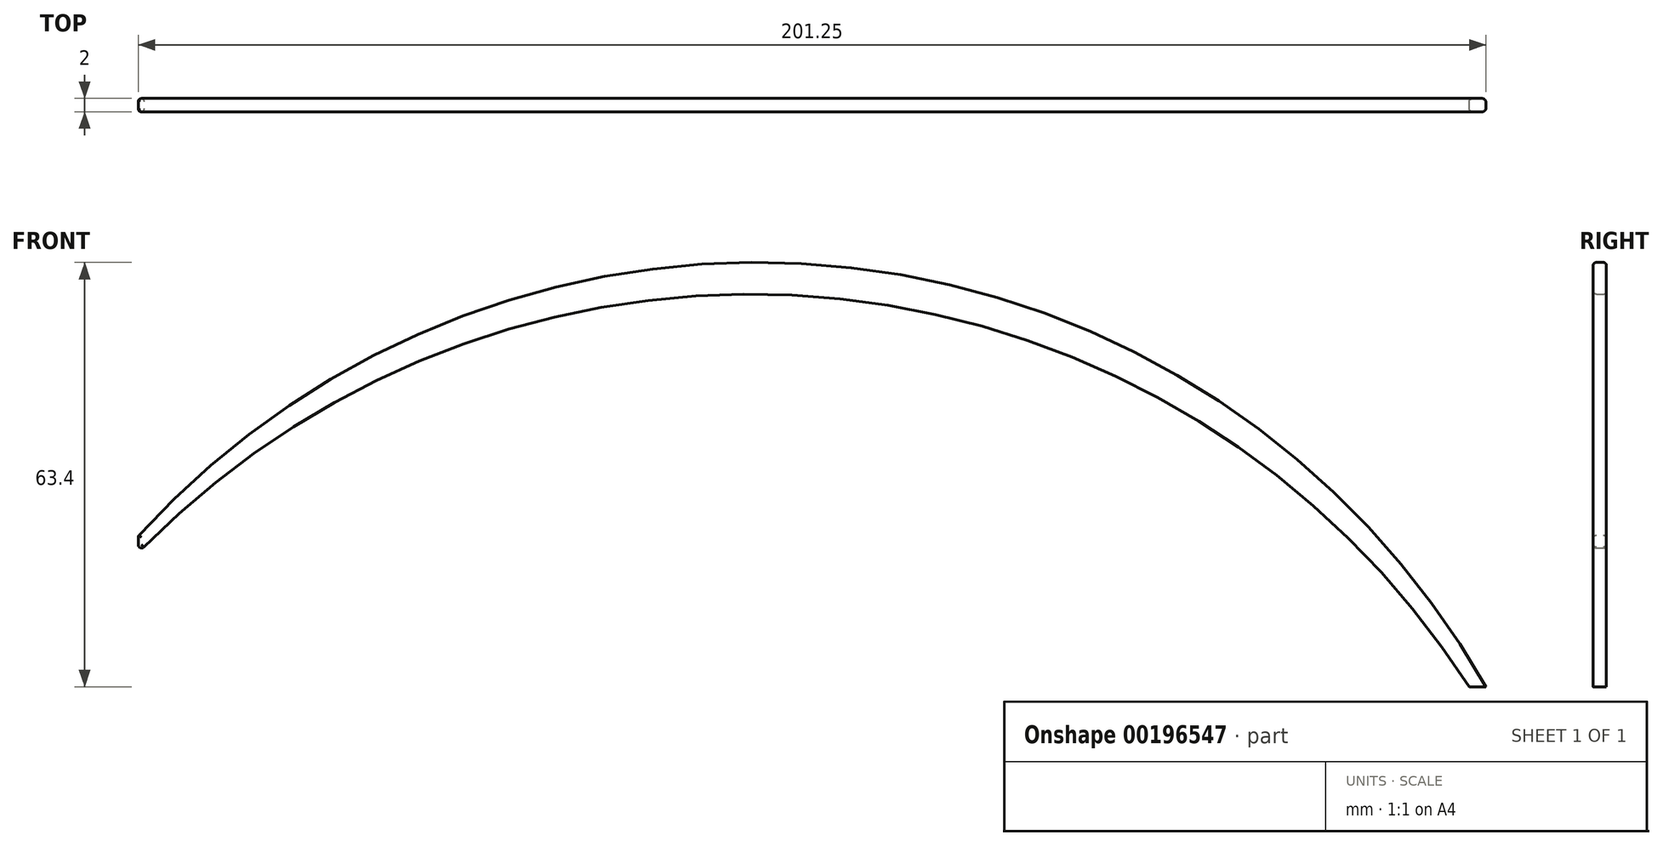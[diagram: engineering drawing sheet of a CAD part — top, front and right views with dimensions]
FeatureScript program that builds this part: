
annotation { "Feature Type Name" : "Feature", "Feature Type Description" : "" }
export const myFeature = defineFeature(function(context is Context, id is Id, definition is map)
    precondition{}
    {
        {
            var Q0;
            Q0=qCreatedBy(makeId("Front.planeOp"),FACE);
            var sketch = newSketch(context, id + "F0", { "sketchPlane" : qUnion([Q0])});
            skLineSegment(sketch, "E0", {"start": v(-1.25, 0) * mm, "end": v(1.25, 0) * mm});
            skLineSegment(sketch, "E1", {"start": v(-200, 22.5) * mm, "end": v(-200, 20) * mm});
            skArc(sketch, "E2", {"start": v(1.25, 0) * mm, "mid": v(-93.63, 62.63) * mm, "end": v(-200, 22.5) * mm});
            skArc(sketch, "E3", {"start": v(-1.25, 0) * mm, "mid": v(-95.8, 58) * mm, "end": v(-200, 20) * mm});
            skSolve(sketch);
        }
        {
            var Q0;
            Q0 = qSketchRegion(id + "F0", true);
            extrude(context, id + "F1", {"entities" : qUnion([Q0]), "depth" : 2 * mm});
        }
        {
            var Q0;
            Q0=makeQuery(id+"F1.opExtrude","CAP_EDGE",EDGE,{"disambiguationData":[OSD([sQuery(id+"F0.wireOp",EDGE,"E2")])],"isStart":false});
            var Q1;
            Q1=makeQuery(id+"F1.opExtrude","CAP_EDGE",EDGE,{"disambiguationData":[OSD([sQuery(id+"F0.wireOp",EDGE,"E3")])],"isStart":false});
            var Q2;
            Q2=makeQuery(id+"F1.opExtrude","CAP_EDGE",EDGE,{"disambiguationData":[OSD([sQuery(id+"F0.wireOp",EDGE,"E2")])],"isStart":true});
            var Q3;
            Q3=makeQuery(id+"F1.opExtrude","CAP_EDGE",EDGE,{"disambiguationData":[OSD([sQuery(id+"F0.wireOp",EDGE,"E3")])],"isStart":true});
            fillet(context, id + "F2", {"entities" : qUnion([Q0, Q1, Q2, Q3]), "radius" : 0.5 * mm, "tangentPropagation" : true, "allowEdgeOverflow" : false});
        }
        {
            var Q0;
            Q0=makeQuery(id+"F1.opExtrude","SWEPT_FACE",FACE,{"disambiguationData":[OSD([sQuery(id+"F0.wireOp",EDGE,"E1")])]});
            fillet(context, id + "F3", {"entities" : qUnion([Q0]), "radius" : 0.5 * mm, "tangentPropagation" : true, "allowEdgeOverflow" : false});
        }
    });
